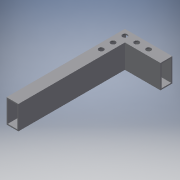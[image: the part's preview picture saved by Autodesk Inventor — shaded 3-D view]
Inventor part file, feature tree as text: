
AUTODESK INVENTOR PART (.ipt)
format: ipt  version: 2018 (Build 220112000, 112)  size: 184,320 bytes
history: native  units: in
note: dims shown in document units (in); Inventor stores cm internally (conversion verified against a paired STEP export)
features: extrude x5, sketch x5
ambient origin geometry x8: Origin, YZ Plane, XZ Plane, XY Plane, X Axis, Y Axis, Z Axis, Center Point
bodies: Body1 (feature_tree)
feature tree (10):
  extrude  "Extrusion12"  Depth=2.0in
  extrude  "Extrusion14"  Depth=0.1in
  extrude  "Extrusion16"  Depth=0.1in
  extrude  "Extrusion17"  Depth=0.1in TaperAngle=0.0deg
  extrude  "Extrusion18"  TaperAngle=0.0deg  [1 undecoded]
  sketch  "Sketch15"  dims[d46=1.0in d47=2.0in]
  sketch  "Sketch17"  dims[d48=0.1in d49=0.1in]
  sketch  "Sketch20"  dims[d50=0.1in d51=0.1in]
  sketch  "Sketch21"  dims[d52=3.0in d53=0.0in d62=0.1in d63=0.0in]
  sketch  "Sketch22"  dims[d71=1.0in d72=2.0in d73=0.1in d74=0.1in d75=0.1in d76=0.1in d77=0.1in d78=0.0in d79=10.0in d80=0.0in d81=0.5in d82=0.5in d83=0.5in d84=1.0in d85=0.5in d86=0.4167in d87=0.4167in d88=0.4167in d89=1.0in d90=1.0in d91=1.0in d92=0.4167in d93=0.4167in d94=0.5in d95=0.5in d96=3.0in d97=0.0in d98=1.0in d99=1.0in d100=0.5in d101=0.5in d102=0.5in d103=0.4167in d104=0.4167in d105=0.4167in d106=3.0in d107=0.0in d108=0.5in]
note: 1 required parameter value undecoded (feature->parameter linkage not recoverable at this tier; creation-order binding heuristic only, values carry confidence <= 0.55)
